# Revit family: Electronics_Visual Electronics_ViewSonic_LS750-850-860WU
name_source: partatom
category: Electrical Equipment
revit_build: Autodesk Revit 2017 (Build: 20171027_0315(x64)
units: mm (PartAtom-declared; Revit-internal decimal feet)

## family parameters
Always vertical = Yes
Cut with Voids When Loaded = No
OmniClass Number = 23.80.00.00
OmniClass Title = Electric Power and Lighting
Panel Configuration = Two Columns, Circuits Across
Part Type = Panelboard
Room Calculation Point = No
Round Connector Dimension = Use Diameter
Shared = No
Work Plane-Based = No

## types (3) — shared parameters
Assembly Code = D50
Brightness = 5000 ANSI Lumens
Contrast Ratio = 3000000:1
Covering Color = Plastic - ViewSonic - White
DMD Type = DC3
Digital Zoom = 0.8x-2.0x
Display Colour = 1.07 Billion Colours
Edition number = 1
HDTV Compatibility = 480i, 480p, 576i, 576p, 720p, 1080i, 1080p
Horizontal Frequency = 15K-102KHz
Input Lag = 16ms
Keynote = 16800
Keystone = H:+/-40° , V:+/-40°
Lamp Watt = Nichia 67W x2
Light Source Life (Normal) = up to 20000
Light Source Type = Laser Phosphor system
Manufacturer = ViewSonic
Native Resolution = 1920x1200
Product data url = https://www.bimobject.com
Projection System = 0.48" WUXGA
Resolution Support = VGA(640 x 480) to WUXGA(1920 x 1200)
URL = https://www.viewsonic.com
Vertical Scan Rate = 23-120Hz
Video Compatibility = NTSC, PAL, SECAM
Zoom = 1
Zoom Control = 1
a = / : "4  - 3"
b = / : "16 - 9"
c = / : "16 - 10"

## per-type parameters (varying)
| type | Audible Noise (Eco) | Audible Noise (Normal) | Description | Diagonal | Diagonal (Zoom) | Height | IAR | Image Aspect Ratio | Image Size | LS750WU | LS850WU | LS860WU | Lens | Lens Shift H. Range | Lens Shift V. Range | Model | Optical Zoom | Product Guid | Projection Distance | Projection Offset | Throw Distance | Throw Ratio | Width |
| LS750WU | 28dB | 35dB | LS750WU - 1920 x 1200 Resolution, 5,000 ANSI Lumens, 1.13-1.47 Throw Ratio

Bright and versatile for any professional installation, the ViewSonic® LS750WU WUXGA laser projector delivers everything you need for big screens in big venues. Delivering 5,000 lumens of advanced high brightness, 300,000:1 contrast ratio, and up to 20,000 hours* of light source life, this projector is ideal for auditoriums, lecture halls, large boardrooms, houses of worship, and more. Thanks to SuperColor™ technology, content is brought to life with captivating color, crisp graphics, and stunning videos no matter the environment. This top-notch performer is also easy to deploy and manage with its wide 1.3x optical zoom adjustment, vertical/horizontal keystone, and 4-corner adjustment that provides extreme flexibility in even the most challenging installations. Moreover, 360-degree tilt angle projection and 24/7 operation allow for extreme mounting flexibility. The ViewSonic® LS750WU is the ideal WUXGA laser projector for professional installations, large venues, and business and education environments.

*Light source life may vary based on actual usage and other factors. | 2056 mm  [stored 6.74541 ft] | 2056 mm  [stored 6.74541 ft] | 1012 mm | 1.768 | / : "16 - 9" | 30"-300" | Yes | No | No | F=1.94-2.06, f=12-15.6mm |  |  | viewsonic_ls750wu_projector | 1.3X | a3e555d7-dd7d-4db9-8459-edb5c06ff180 | 2025 mm | 100%+/-5% | 0.73-9.50m (100"@2.43m) | 1.13-1.47 | 1790 mm |
| LS850WU | 29dB | 36dB | LS850WU - 1920 x 1200 Resolution, 5,000 ANSI Lumens, 1.36 - 2.18 Throw Ratio

Bright and versatile for any professional installation, the ViewSonic® LS850WU WUXGA laser projector delivers everything you need for big screens in big venues. Delivering 5,000 lumens of advanced high brightness, 300,000:1 contrast ratio, and up to 20,000 hours* of light source life, this projector is ideal for auditoriums, lecture halls, large boardrooms, houses of worship, and more. Thanks to SuperColor™ technology, content is brought to life with captivating color, crisp graphics, and stunning videos no matter the environment. This top-notch performer is also easy to deploy and manage with its wide 1.6x optical zoom adjustment, vertical/horizontal keystone, 4 corner adjustment, and a vertical/horizontal lens shift feature that provide extreme flexibility in even the most challenging installations. Thanks to the built-in HDBT receiver, the projector is capable of receiving uncompressed HD video and audio from over 200 feet away via network cable. Moreover, 360-degree tilt angle projection, portrait mode, and 24/7 operation allow for extreme mounting flexibility. The ViewSonic® LS850WU is the ideal WUXGA laser projector for professional installations, large venues, and business and education environments.

*Light source life may vary based on actual usage and other factors. | 2056 mm  [stored 6.74541 ft] | 2056 mm  [stored 6.74541 ft] | 1232 mm | 1.33552 | / : "4  - 3" | 30"-300" | No | Yes | No | F=1.81-2.1, f=14.3-22.9mm | Yes (+23%, -23%) | Yes (+50%, -50%) | viewsonic_ls850wu_projector | 1.6X | a9adb598-bb25-4bd1-881a-e97012c2a03f | 2237 mm | 0 | 0.88-14.09m (100"@2.93m) | 1.36-2.18 | 1646 mm |
| LS860WU | 29dB | 36dB | LS860WU - 1920 x 1200 Resolution, 5,000 ANSI Lumens, 0.81 - 0.89 Throw Ratio

Bright and versatile for any professional installation, the ViewSonic® LS860WU WUXGA laser projector delivers everything you need for big screens in big venues. Delivering 5,000 lumens of advanced high brightness, 300,000:1 contrast ratio, and up to 20,000 hours* of light source life, this projector is ideal for auditoriums, lecture halls, large boardrooms, houses of worship, and more. Thanks to SuperColor™ technology, content is brought to life with captivating color, crisp graphics, and stunning videos no matter the environment. This top-notch performer is also easy to deploy and manage with its vertical/horizontal keystone, 4-corner adjustment, and a vertical/horizontal lens shift feature that provides extreme flexibility in even the most challenging installations. A short throw lens with a 0.8 throw ratio offers large projection images for smaller rooms. Thanks to the built-in HDBT receiver, the projector is capable of receiving uncompressed HD video and audio from over 200 feet away via network cable. Moreover, 360-degree tilt angle projection, portrait mode, and 24/7 operation allow for extreme mounting flexibility. The ViewSonic® LS860WU is the ideal WUXGA laser projector for professional installations, large venues, and business and education environments.

*Light source life may vary based on actual usage and other f | 3026 mm  [stored 9.92782 ft] | 3026 mm  [stored 9.92782 ft] | 1490 mm | 1.768 | / : "16 - 9" | 60"-200" | No | No | Yes | F=1.83-1.86, f=9.6-9.4mm | Yes (+23%, -23%) | Yes (+50%, -50%) | viewsonic_ls860wu_projector | 1.1X | 98f41182-b75b-4743-9e17-ecdc0dc0f9ca | 2136 mm | 0 | 1.04-3.83m (100"@1.74m) | 0.81-0.89 | 2634 mm |

note: [stored X ft] marks values corroborated as IEEE doubles in the binary element streams (Revit-internal decimal feet)

## geometry (parser evidence)
native form markers: Sweep x17
no freeform markers — native parametric forms only
